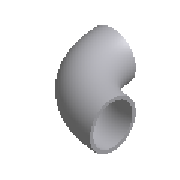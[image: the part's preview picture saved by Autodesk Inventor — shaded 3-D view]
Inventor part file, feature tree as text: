
AUTODESK INVENTOR PART (.ipt)
format: ipt  version: 2023.2 (Build 272271030, 271C)  size: 185,856 bytes
history: native  units: mm (DEFAULTED — no unit token found)
features: other x4, sketch x2, sweep x1
ambient origin geometry x8: Origin, YZ Plane, XZ Plane, XY Plane, X Axis, Y Axis, Z Axis, Center Point
bodies: Solid1 (feature_tree)
feature tree (7):
  sweep  "Sweep1"
  other  "Work Point1"
  other  "Work Point2"
  other  "Work Axis1"
  other  "Work Axis2"
  sketch  "Sketch1"  dims[d0=23.7mm d1=26.9mm]
  sketch  "Sketch2"  dims[d2=29.0mm d3=29.0mm d4=0.0mm d5=0.0mm]
